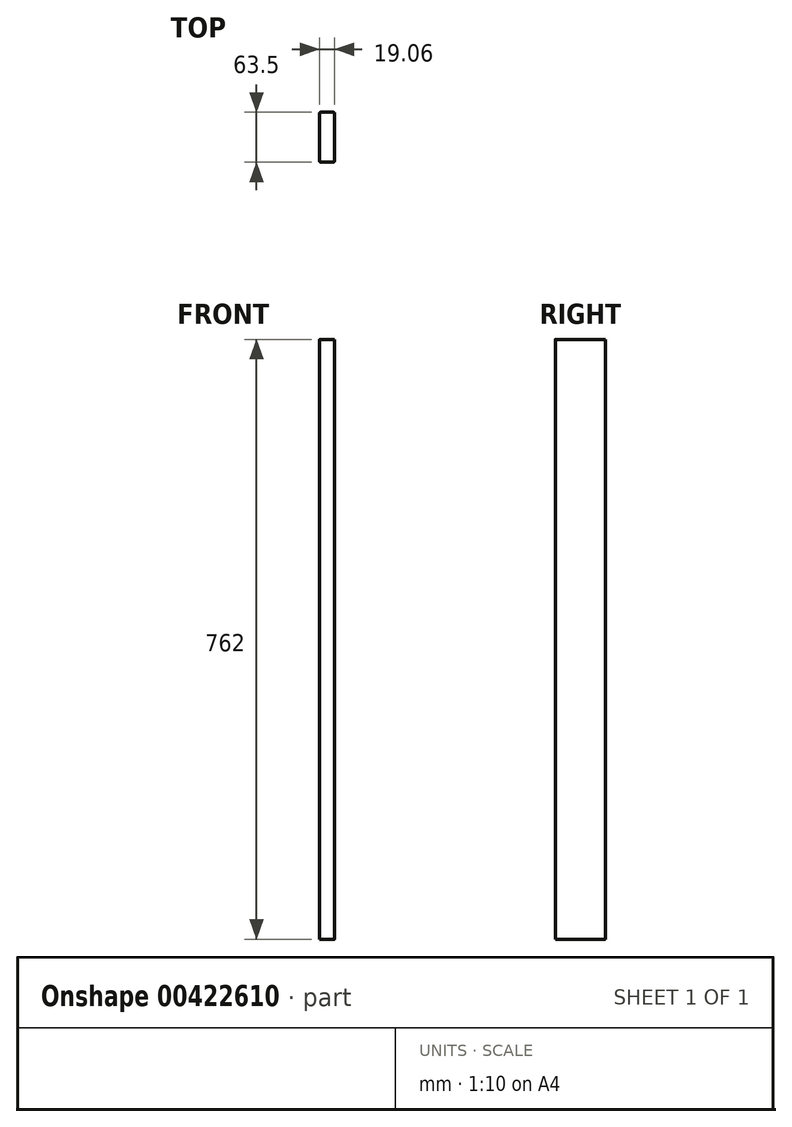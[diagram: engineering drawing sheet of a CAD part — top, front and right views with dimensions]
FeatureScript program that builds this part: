
annotation { "Feature Type Name" : "Feature", "Feature Type Description" : "" }
export const myFeature = defineFeature(function(context is Context, id is Id, definition is map)
    precondition{}
    {
        {
            var Q0;
            Q0=qCreatedBy(makeId("Top.planeOp"),FACE);
            var sketch = newSketch(context, id + "F0", { "sketchPlane" : qUnion([Q0])});
            skLineSegment(sketch, "E0", {"start": v(0, 31.75) * mm, "end": v(0, -31.75) * mm, "construction": true});
            skLineSegment(sketch, "E1", {"start": v(-9.52, 0) * mm, "end": v(9.53, 0) * mm, "construction": true});
            skLineSegment(sketch, "E2.bottom", {"start": v(-7.94, 31.75) * mm, "end": v(7.94, 31.75) * mm});
            skLineSegment(sketch, "E2.top", {"start": v(-7.94, -31.75) * mm, "end": v(7.94, -31.75) * mm});
            skLineSegment(sketch, "E2.left", {"start": v(-9.52, 30.16) * mm, "end": v(-9.52, -30.16) * mm});
            skLineSegment(sketch, "E2.right", {"start": v(9.53, 30.16) * mm, "end": v(9.53, -30.16) * mm});
            skPoint(sketch, "E3.visualSharp", {"position": v(-9.52, 31.75) * mm});
            skArc(sketch, "E3.filletArc", {"start": v(-7.94, 31.75) * mm, "mid": v(-9.06, 31.29) * mm, "end": v(-9.52, 30.16) * mm});
            skPoint(sketch, "E4.visualSharp", {"position": v(9.53, 31.75) * mm});
            skArc(sketch, "E4.filletArc", {"start": v(9.53, 30.16) * mm, "mid": v(9.06, 31.29) * mm, "end": v(7.94, 31.75) * mm});
            skPoint(sketch, "E5.visualSharp", {"position": v(9.53, -31.75) * mm});
            skArc(sketch, "E5.filletArc", {"start": v(7.94, -31.75) * mm, "mid": v(9.06, -31.29) * mm, "end": v(9.53, -30.16) * mm});
            skPoint(sketch, "E6.visualSharp", {"position": v(-9.52, -31.75) * mm});
            skArc(sketch, "E6.filletArc", {"start": v(-9.52, -30.16) * mm, "mid": v(-9.06, -31.29) * mm, "end": v(-7.94, -31.75) * mm});
            skSolve(sketch);
        }
        {
            var Q0;
            Q0=makeQuery(id+"F0.imprint","IMPRINT",FACE,{"disambiguationData":[TD([[makeQuery(id+"F0.imprint","IMPRINT",EDGE,{"derivedFrom":sQuery(id+"F0.wireOp",EDGE,"E2.bottom")}),-1.0]])]});
            extrude(context, id + "F1", {"entities" : qUnion([Q0]), "depth" : 762 * mm});
        }
    });
